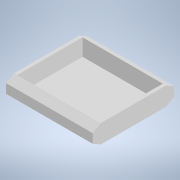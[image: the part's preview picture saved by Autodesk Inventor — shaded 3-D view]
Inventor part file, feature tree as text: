
AUTODESK INVENTOR PART (.ipt)
format: ipt  version: 2020 (Build 240168000, 168)  size: 120,832 bytes
history: native  units: in
note: dims shown in document units (in); Inventor stores cm internally (conversion verified against a paired STEP export)
features: extrude x2, sketch x2, projected_geometry x1
ambient origin geometry x8: Origin, YZ Plane, XZ Plane, XY Plane, X Axis, Y Axis, Z Axis, Center Point
bodies: Solid1 (feature_tree)
feature tree (5):
  extrude  "Extrusion1"  Depth=5.9055in
  extrude  "Extrusion2"  TaperAngle=0.0deg  [1 undecoded]
  sketch  "Sketch1"  dims[d0=1.3386in d1=5.9055in]
  sketch  "Sketch2"  dims[d2=6.2992in d3=0.0in d4=0.2362in d5=1.2205in d6=0.0in]
  projected_geometry  "Projected Loop1"
note: 1 required parameter value undecoded (feature->parameter linkage not recoverable at this tier; creation-order binding heuristic only, values carry confidence <= 0.55)
